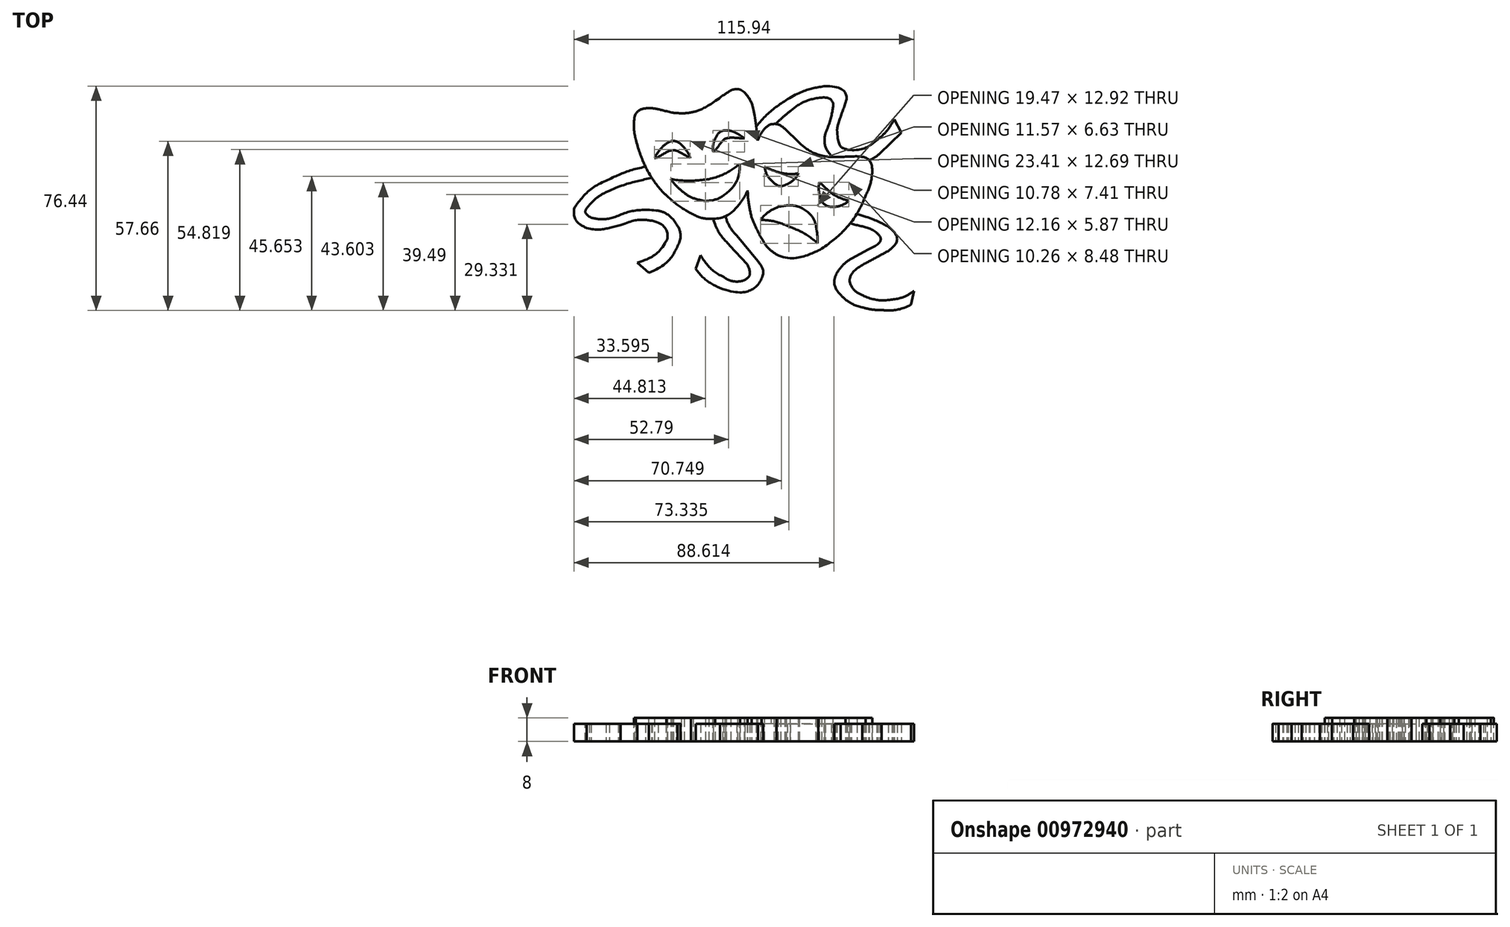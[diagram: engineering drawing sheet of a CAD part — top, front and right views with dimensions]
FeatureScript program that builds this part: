
annotation { "Feature Type Name" : "Feature", "Feature Type Description" : "" }
export const myFeature = defineFeature(function(context is Context, id is Id, definition is map)
    precondition{}
    {
        {
            var Q0;
            Q0=qCreatedBy(makeId("Top.planeOp"),FACE);
            var sketch = newSketch(context, id + "F0", { "sketchPlane" : qUnion([Q0])});
            skFitSpline(sketch, "E0", {"points": [v(-36.35, 12.89) * mm, v(-41.05, 10.12) * mm], "startDerivative": vector(-3.86, -0.6) * mm, "endDerivative": vector(-3.7, -8.46) * mm});
            skFitSpline(sketch, "E1", {"points": [v(-36.35, 12.89) * mm, v(-28.3, 11.3) * mm], "startDerivative": vector(6.38, 0) * mm, "endDerivative": vector(11.28, -3.12) * mm});
            skFitSpline(sketch, "E2", {"points": [v(-28.3, 11.3) * mm, v(-21.02, 11.6) * mm], "startDerivative": vector(6.97, -0.45) * mm, "endDerivative": vector(7.42, 2.23) * mm});
            skFitSpline(sketch, "E3", {"points": [v(-21.02, 11.6) * mm, v(-10.98, 17.14) * mm], "startDerivative": vector(5.93, 0.6) * mm, "endDerivative": vector(14.84, 11.13) * mm});
            skFitSpline(sketch, "E4", {"points": [v(-10.98, 17.14) * mm, v(-3.61, 18.33) * mm], "startDerivative": vector(6.53, 3.86) * mm, "endDerivative": vector(9.64, -7.27) * mm});
            skFitSpline(sketch, "E5", {"points": [v(-3.61, 18.33) * mm, v(0.49, 5.72) * mm], "startDerivative": vector(7.71, -9.5) * mm, "endDerivative": vector(2.67, -25.37) * mm});
            skFitSpline(sketch, "E6", {"points": [v(0.49, 5.72) * mm, v(-0.6, -9.66) * mm], "startDerivative": vector(2.52, -15.28) * mm, "endDerivative": vector(-5.04, -15.58) * mm});
            skFitSpline(sketch, "E7", {"points": [v(-0.6, -9.66) * mm, v(-5.05, -19.55) * mm], "startDerivative": vector(-3.26, -11.13) * mm, "endDerivative": vector(-6.97, -9.05) * mm});
            skFitSpline(sketch, "E8", {"points": [v(-5.05, -19.55) * mm, v(-13.56, -24.85) * mm], "startDerivative": vector(-6.38, -7.57) * mm, "endDerivative": vector(-14.24, -1.48) * mm});
            skFitSpline(sketch, "E9", {"points": [v(-13.56, -24.85) * mm, v(-21.86, -22.92) * mm], "startDerivative": vector(-8.75, -0.45) * mm, "endDerivative": vector(-9.2, 5.79) * mm});
            skFitSpline(sketch, "E10", {"points": [v(-21.86, -22.92) * mm, v(-30.27, -16.83) * mm], "startDerivative": vector(-7.57, 3.56) * mm, "endDerivative": vector(-9.35, 8.75) * mm});
            skFitSpline(sketch, "E11", {"points": [v(-30.27, -16.83) * mm, v(-36.85, -8.08) * mm], "startDerivative": vector(-5.2, 4.6) * mm, "endDerivative": vector(-7.71, 14.24) * mm});
            skFitSpline(sketch, "E12", {"points": [v(-36.85, -8.08) * mm, v(-40.66, 2.26) * mm], "startDerivative": vector(-2.23, 4.15) * mm, "endDerivative": vector(-3.41, 14.4) * mm});
            skFitSpline(sketch, "E13", {"points": [v(-40.66, 2.26) * mm, v(-41.05, 10.12) * mm], "startDerivative": vector(-0.6, 1.78) * mm, "endDerivative": vector(1.78, 13.2) * mm});
            skSolve(sketch);
        }
        {
            var Q0;
            Q0=qCreatedBy(makeId("Top.planeOp"),FACE);
            var sketch = newSketch(context, id + "F1", { "sketchPlane" : qUnion([Q0])});
            skFitSpline(sketch, "E14", {"points": [v(-34.23, -4.2) * mm, v(-29.9, 0.99) * mm], "startDerivative": vector(3.98, 9.03) * mm, "endDerivative": vector(1.64, 0.6) * mm});
            skFitSpline(sketch, "E15", {"points": [v(-29.9, 0.99) * mm, v(-25.1, 0.39) * mm], "startDerivative": vector(6.69, 4.94) * mm, "endDerivative": vector(1.32, -1.72) * mm});
            skFitSpline(sketch, "E16", {"points": [v(-25.1, 0.39) * mm, v(-22.07, -4.1) * mm], "startDerivative": vector(4.23, -3.83) * mm, "endDerivative": vector(1.19, -3.97) * mm});
            skFitSpline(sketch, "E17", {"points": [v(-22.07, -4.1) * mm, v(-27.75, -1.5) * mm], "startDerivative": vector(-7.14, 3.44) * mm, "endDerivative": vector(-3.57, -0.53) * mm});
            skFitSpline(sketch, "E18", {"points": [v(-27.75, -1.5) * mm, v(-34.23, -4.2) * mm], "startDerivative": vector(-5.15, 1.19) * mm, "endDerivative": vector(-5.7, -0.83) * mm});
            skFitSpline(sketch, "E19", {"points": [v(-14.22, -2.12) * mm, v(-13.52, 2.55) * mm], "startDerivative": vector(-0.66, 2.51) * mm, "endDerivative": vector(2.78, 4.76) * mm});
            skFitSpline(sketch, "E20", {"points": [v(-13.52, 2.55) * mm, v(-10.26, 5.23) * mm], "startDerivative": vector(3.04, 7.14) * mm, "endDerivative": vector(2.78, 0) * mm});
            skFitSpline(sketch, "E21", {"points": [v(-10.26, 5.23) * mm, v(-5.94, 4.18) * mm], "startDerivative": vector(4.36, 0.66) * mm, "endDerivative": vector(3.83, -2.25) * mm});
            skFitSpline(sketch, "E22", {"points": [v(-5.94, 4.18) * mm, v(-3.56, 2.55) * mm], "startDerivative": vector(2.64, -1.72) * mm, "endDerivative": vector(2.38, -1.63) * mm});
            skFitSpline(sketch, "E23", {"points": [v(-3.56, 2.55) * mm, v(-9.82, 2.55) * mm], "startDerivative": vector(-6.26, 0) * mm, "endDerivative": vector(-5.68, -1.72) * mm});
            skFitSpline(sketch, "E24", {"points": [v(-9.82, 2.55) * mm, v(-14.22, -2.12) * mm], "startDerivative": vector(-3.83, -0.4) * mm, "endDerivative": vector(-3.17, -1.85) * mm});
            skFitSpline(sketch, "E25", {"points": [v(-28.63, -11.29) * mm, v(-15.72, -11.33) * mm], "startDerivative": vector(12.95, -2.78) * mm, "endDerivative": vector(13.48, 1.85) * mm});
            skFitSpline(sketch, "E26", {"points": [v(-15.72, -11.33) * mm, v(-5.23, -6.13) * mm], "startDerivative": vector(14.8, 3.3) * mm, "endDerivative": vector(8.72, 7.14) * mm});
            skFitSpline(sketch, "E27", {"points": [v(-5.23, -6.13) * mm, v(-8.27, -14.81) * mm], "startDerivative": vector(1.06, -15.2) * mm, "endDerivative": vector(-2.9, -2.51) * mm});
            skFitSpline(sketch, "E28", {"points": [v(-8.27, -14.81) * mm, v(-16.87, -18.82) * mm], "startDerivative": vector(-9.25, -9.12) * mm, "endDerivative": vector(-11.37, -0.8) * mm});
            skFitSpline(sketch, "E29", {"points": [v(-16.87, -18.82) * mm, v(-24.18, -16) * mm], "startDerivative": vector(-13.22, 2.25) * mm, "endDerivative": vector(-5.55, 4.1) * mm});
            skFitSpline(sketch, "E30", {"points": [v(-24.18, -16) * mm, v(-28.63, -11.29) * mm], "startDerivative": vector(-6.87, 5.55) * mm, "endDerivative": vector(-2.38, 4.23) * mm});
            skSolve(sketch);
        }
        {
            var Q0;
            Q0=qCreatedBy(makeId("Top.planeOp"),FACE);
            var sketch = newSketch(context, id + "F2", { "sketchPlane" : qUnion([Q0])});
            skFitSpline(sketch, "E31", {"points": [v(5.5, 7.38) * mm, v(0.42, 0.67) * mm], "startDerivative": vector(-8.96, -3.46) * mm, "endDerivative": vector(-2.68, -6.3) * mm});
            skFitSpline(sketch, "E32", {"points": [v(0.42, 0.67) * mm, v(-2.35, -11.38) * mm], "startDerivative": vector(-5.97, -11.78) * mm, "endDerivative": vector(-0.79, -6.9) * mm});
            skFitSpline(sketch, "E33", {"points": [v(-2.35, -11.38) * mm, v(-1.13, -24.42) * mm], "startDerivative": vector(-1.41, -14.94) * mm, "endDerivative": vector(2.87, -10.99) * mm});
            skFitSpline(sketch, "E34", {"points": [v(-1.13, -24.42) * mm, v(2.25, -31.53) * mm], "startDerivative": vector(3.39, -7.1) * mm, "endDerivative": vector(4.86, -8.1) * mm});
            skFitSpline(sketch, "E35", {"points": [v(2.25, -31.53) * mm, v(7.36, -37.02) * mm], "startDerivative": vector(5.83, -10.76) * mm, "endDerivative": vector(5.88, -4) * mm});
            skFitSpline(sketch, "E36", {"points": [v(7.36, -37.02) * mm, v(21.6, -35.7) * mm], "startDerivative": vector(17.86, -9.21) * mm, "endDerivative": vector(7.86, 3.3) * mm});
            skFitSpline(sketch, "E37", {"points": [v(21.6, -35.7) * mm, v(30.84, -28.25) * mm], "startDerivative": vector(13.83, 8.02) * mm, "endDerivative": vector(1.5, 2.67) * mm});
            skFitSpline(sketch, "E38", {"points": [v(30.84, -28.25) * mm, v(37.73, -16.99) * mm], "startDerivative": vector(12.49, 13.2) * mm, "endDerivative": vector(3.14, 8.02) * mm});
            skFitSpline(sketch, "E39", {"points": [v(37.73, -16.99) * mm, v(39.98, -8.66) * mm], "startDerivative": vector(4.4, 8.33) * mm, "endDerivative": vector(0, 7.23) * mm});
            skFitSpline(sketch, "E40", {"points": [v(39.98, -8.66) * mm, v(34.85, -3.58) * mm], "startDerivative": vector(0.79, 16.5) * mm, "endDerivative": vector(-2.83, 0.47) * mm});
            skFitSpline(sketch, "E41", {"points": [v(34.85, -3.58) * mm, v(23.74, -3.58) * mm], "startDerivative": vector(-11.42, 0) * mm, "endDerivative": vector(-10.85, 1.57) * mm});
            skFitSpline(sketch, "E42", {"points": [v(23.74, -3.58) * mm, v(14.94, 1.14) * mm], "startDerivative": vector(-13.2, 2.83) * mm, "endDerivative": vector(-6.76, 5.97) * mm});
            skFitSpline(sketch, "E43", {"points": [v(14.94, 1.14) * mm, v(10.12, 5.9) * mm], "startDerivative": vector(-4.82, 4.77) * mm, "endDerivative": vector(-4.82, 4.77) * mm});
            skFitSpline(sketch, "E44", {"points": [v(10.12, 5.9) * mm, v(5.5, 7.38) * mm], "startDerivative": vector(-4.09, 3.46) * mm, "endDerivative": vector(-7.07, -1.1) * mm});
            skSolve(sketch);
        }
        {
            var Q0;
            Q0=qCreatedBy(makeId("Top.planeOp"),FACE);
            var sketch = newSketch(context, id + "F3", { "sketchPlane" : qUnion([Q0])});
            skFitSpline(sketch, "E45", {"points": [v(3.22, -7.11) * mm, v(8.84, -9.23) * mm], "startDerivative": vector(4, -1.87) * mm, "endDerivative": vector(5.24, -1.25) * mm});
            skFitSpline(sketch, "E46", {"points": [v(8.84, -9.23) * mm, v(14.8, -9.36) * mm], "startDerivative": vector(7.36, -1.25) * mm, "endDerivative": vector(5.9, 1.25) * mm});
            skFitSpline(sketch, "E47", {"points": [v(14.8, -9.36) * mm, v(10.74, -13.2) * mm], "startDerivative": vector(-1.16, -3.62) * mm, "endDerivative": vector(-7.39, -3.68) * mm});
            skFitSpline(sketch, "E48", {"points": [v(10.74, -13.2) * mm, v(6.5, -12.68) * mm], "startDerivative": vector(-4.21, -1.43) * mm, "endDerivative": vector(-5.64, 4.95) * mm});
            skFitSpline(sketch, "E49", {"points": [v(32, -18.66) * mm, v(26.55, -16.42) * mm], "startDerivative": vector(-7.24, 1.58) * mm, "endDerivative": vector(-4.63, 3.01) * mm});
            skFitSpline(sketch, "E50", {"points": [v(26.55, -16.42) * mm, v(21.98, -12.35) * mm], "startDerivative": vector(-5.1, 3.6) * mm, "endDerivative": vector(-4.4, 3.85) * mm});
            skFitSpline(sketch, "E51", {"points": [v(21.98, -12.35) * mm, v(22.77, -18.8) * mm], "startDerivative": vector(-1.73, -6.7) * mm, "endDerivative": vector(2.38, -3.75) * mm});
            skFitSpline(sketch, "E52", {"points": [v(22.77, -18.8) * mm, v(27.04, -20.83) * mm], "startDerivative": vector(3.11, -5.73) * mm, "endDerivative": vector(4.82, -0.1) * mm});
            skFitSpline(sketch, "E53", {"points": [v(27.04, -20.83) * mm, v(32, -18.66) * mm], "startDerivative": vector(6.28, 0.6) * mm, "endDerivative": vector(3, 3.53) * mm});
            skFitSpline(sketch, "E54", {"points": [v(1.86, -25.3) * mm, v(7.94, -20.83) * mm], "startDerivative": vector(6.1, 8.54) * mm, "endDerivative": vector(4.55, 1.9) * mm});
            skFitSpline(sketch, "E55", {"points": [v(7.94, -20.83) * mm, v(15.07, -20.84) * mm], "startDerivative": vector(10.17, 2.6) * mm, "endDerivative": vector(4.28, -1.72) * mm});
            skFitSpline(sketch, "E56", {"points": [v(20.69, -26.66) * mm, v(21.3, -33.2) * mm], "startDerivative": vector(2.25, -11.35) * mm, "endDerivative": vector(-0.16, -4.05) * mm});
            skFitSpline(sketch, "E57", {"points": [v(21.3, -33.2) * mm, v(11.93, -27.61) * mm], "startDerivative": vector(-8.7, 8.54) * mm, "endDerivative": vector(-9.69, 3.75) * mm});
            skFitSpline(sketch, "E58", {"points": [v(11.93, -27.61) * mm, v(1.86, -25.3) * mm], "startDerivative": vector(-10.52, 4.48) * mm, "endDerivative": vector(-9.96, -0.56) * mm});
            skFitSpline(sketch, "E59", {"points": [v(15.07, -20.84) * mm, v(20.69, -26.66) * mm], "startDerivative": vector(12.48, -5.49) * mm, "endDerivative": vector(2, -5.61) * mm});
            skFitSpline(sketch, "E60", {"points": [v(6.5, -12.68) * mm, v(3.22, -7.11) * mm], "startDerivative": vector(-6.86, 6.39) * mm, "endDerivative": vector(-1.9, 8.17) * mm});
            skSolve(sketch);
        }
        {
            var Q0;
            Q0 = qSketchRegion(id + "F0", true);
            extrude(context, id + "F4", {"entities" : qUnion([Q0]), "depth" : 8 * mm, "offsetDistance" : 25.4 * mm});
        }
        {
            var Q0;
            Q0 = qSketchRegion(id + "F1", true);
            extrude(context, id + "F5", {"entities" : qUnion([Q0]), "operationType" : NewBodyOperationType.REMOVE, "depth" : 25 * mm, "offsetDistance" : 25 * mm});
        }
        {
            var Q0;
            Q0 = qSketchRegion(id + "F2", true);
            extrude(context, id + "F6", {"entities" : qUnion([Q0]), "operationType" : NewBodyOperationType.ADD, "depth" : 8 * mm, "offsetDistance" : 25 * mm});
        }
        {
            var Q0;
            Q0 = qSketchRegion(id + "F3", true);
            extrude(context, id + "F7", {"entities" : qUnion([Q0]), "operationType" : NewBodyOperationType.REMOVE, "depth" : 25 * mm, "offsetDistance" : 25 * mm});
        }
        {
            var Q0;
            Q0=qCreatedBy(makeId("Top.planeOp"),FACE);
            var sketch = newSketch(context, id + "F8", { "sketchPlane" : qUnion([Q0])});
            skFitSpline(sketch, "E61", {"points": [v(33.8, -22.83) * mm, v(46.72, -28.6) * mm], "startDerivative": vector(21.4, -6.89) * mm, "endDerivative": vector(8.2, -6.74) * mm});
            skFitSpline(sketch, "E62", {"points": [v(33.8, -22.83) * mm, v(31.78, -26.2) * mm], "startDerivative": vector(-2.01, -3.38) * mm, "endDerivative": vector(-2.01, -3.38) * mm});
            skFitSpline(sketch, "E63", {"points": [v(31.78, -26.2) * mm, v(41.6, -29.65) * mm], "startDerivative": vector(9.81, -3.44) * mm, "endDerivative": vector(8.56, -6.85) * mm});
            skFitSpline(sketch, "E64", {"points": [v(41.6, -29.65) * mm, v(38.8, -35.24) * mm], "startDerivative": vector(5.35, -5.2) * mm, "endDerivative": vector(-15.81, -6.92) * mm});
            skFitSpline(sketch, "E65", {"points": [v(38.8, -35.24) * mm, v(32.88, -38.42) * mm], "startDerivative": vector(-5.91, -3.18) * mm, "endDerivative": vector(-5.91, -3.18) * mm});
            skFitSpline(sketch, "E66", {"points": [v(32.88, -38.42) * mm, v(27.75, -43.62) * mm], "startDerivative": vector(-6.06, -3.65) * mm, "endDerivative": vector(-4.53, -7.79) * mm});
            skFitSpline(sketch, "E67", {"points": [v(27.75, -43.62) * mm, v(29.18, -50.76) * mm], "startDerivative": vector(-2.48, -5.56) * mm, "endDerivative": vector(8.95, -8.88) * mm});
            skFitSpline(sketch, "E68", {"points": [v(29.18, -50.76) * mm, v(36.59, -55.05) * mm], "startDerivative": vector(5.27, -5.56) * mm, "endDerivative": vector(10.6, -2.28) * mm});
            skFitSpline(sketch, "E69", {"points": [v(36.59, -55.05) * mm, v(43.15, -56.03) * mm], "startDerivative": vector(7.12, -2.1) * mm, "endDerivative": vector(7.76, -0.17) * mm});
            skFitSpline(sketch, "E70", {"points": [v(43.15, -56.03) * mm, v(53.29, -54.08) * mm], "startDerivative": vector(7.12, 0.17) * mm, "endDerivative": vector(14.1, 7.87) * mm});
            skFitSpline(sketch, "E71", {"points": [v(53.29, -54.08) * mm, v(54.2, -49.53) * mm], "startDerivative": vector(0.9, 4.55) * mm, "endDerivative": vector(0.9, 4.55) * mm});
            skFitSpline(sketch, "E72", {"points": [v(54.2, -49.53) * mm, v(47.3, -52.32) * mm], "startDerivative": vector(-5.45, -3.35) * mm, "endDerivative": vector(-11.05, -1.3) * mm});
            skFitSpline(sketch, "E73", {"points": [v(47.3, -52.32) * mm, v(37.24, -51.22) * mm], "startDerivative": vector(-10.39, -1.54) * mm, "endDerivative": vector(-12.6, 5.29) * mm});
            skFitSpline(sketch, "E74", {"points": [v(37.24, -51.22) * mm, v(32.24, -46.15) * mm], "startDerivative": vector(-7.3, 3.9) * mm, "endDerivative": vector(-3.33, 10.86) * mm});
            skFitSpline(sketch, "E75", {"points": [v(32.24, -46.15) * mm, v(37.89, -39.91) * mm], "startDerivative": vector(0.27, 5.1) * mm, "endDerivative": vector(14.94, 7.7) * mm});
            skFitSpline(sketch, "E76", {"points": [v(37.89, -39.91) * mm, v(45.45, -35.84) * mm], "startDerivative": vector(7.8, 4.22) * mm, "endDerivative": vector(7.8, 4.22) * mm});
            skFitSpline(sketch, "E77", {"points": [v(45.45, -35.84) * mm, v(46.72, -28.6) * mm], "startDerivative": vector(2.63, 2.4) * mm, "endDerivative": vector(-12.6, 11.64) * mm});
            skSolve(sketch);
        }
        {
            var Q0;
            Q0=qCreatedBy(makeId("Top.planeOp"),FACE);
            var sketch = newSketch(context, id + "F9", { "sketchPlane" : qUnion([Q0])});
            skFitSpline(sketch, "E78", {"points": [v(-35.88, -6.89) * mm, v(-34.36, -10.54) * mm], "startDerivative": vector(1.51, -3.65) * mm, "endDerivative": vector(1.51, -3.65) * mm});
            skFitSpline(sketch, "E79", {"points": [v(-34.36, -10.54) * mm, v(-49.64, -15.3) * mm], "startDerivative": vector(-15.27, -4.76) * mm, "endDerivative": vector(-18.02, -8.7) * mm});
            skFitSpline(sketch, "E80", {"points": [v(-49.64, -15.3) * mm, v(-56.46, -20.17) * mm], "startDerivative": vector(-8.05, -3.3) * mm, "endDerivative": vector(-7, -8) * mm});
            skFitSpline(sketch, "E81", {"points": [v(-56.46, -20.17) * mm, v(-55.82, -24.45) * mm], "startDerivative": vector(-3.85, -4.52) * mm, "endDerivative": vector(9.79, -5.03) * mm});
            skFitSpline(sketch, "E82", {"points": [v(-55.82, -24.45) * mm, v(-46.62, -23.8) * mm], "startDerivative": vector(7.17, -2.08) * mm, "endDerivative": vector(11.72, 5.05) * mm});
            skFitSpline(sketch, "E83", {"points": [v(-46.62, -23.8) * mm, v(-32.98, -22.11) * mm], "startDerivative": vector(12.42, 5.57) * mm, "endDerivative": vector(18.18, -2.06) * mm});
            skFitSpline(sketch, "E84", {"points": [v(-32.98, -22.11) * mm, v(-26.92, -26.56) * mm], "startDerivative": vector(5.07, -1.21) * mm, "endDerivative": vector(5.93, -10.07) * mm});
            skFitSpline(sketch, "E85", {"points": [v(-26.92, -26.56) * mm, v(-26.35, -34.09) * mm], "startDerivative": vector(3.14, -3.82) * mm, "endDerivative": vector(-5.95, -10.78) * mm});
            skFitSpline(sketch, "E86", {"points": [v(-26.35, -34.09) * mm, v(-36.15, -43.3) * mm], "startDerivative": vector(-5.6, -11.3) * mm, "endDerivative": vector(-21.51, -9.4) * mm});
            skFitSpline(sketch, "E87", {"points": [v(-36.15, -43.3) * mm, v(-40.1, -39.84) * mm], "startDerivative": vector(-3.96, 3.47) * mm, "endDerivative": vector(-3.96, 3.47) * mm});
            skFitSpline(sketch, "E88", {"points": [v(-40.1, -39.84) * mm, v(-30.3, -32.53) * mm], "startDerivative": vector(8.04, 3.14) * mm, "endDerivative": vector(8.76, 16.68) * mm});
            skFitSpline(sketch, "E89", {"points": [v(-30.3, -32.53) * mm, v(-35.02, -25.53) * mm], "startDerivative": vector(2.27, 2.26) * mm, "endDerivative": vector(-18.88, 3.8) * mm});
            skFitSpline(sketch, "E90", {"points": [v(-35.02, -25.53) * mm, v(-45.8, -27.05) * mm], "startDerivative": vector(-9.61, 1.2) * mm, "endDerivative": vector(-17.66, -7.49) * mm});
            skFitSpline(sketch, "E91", {"points": [v(-45.8, -27.05) * mm, v(-57.4, -27.99) * mm], "startDerivative": vector(-12.94, -2.62) * mm, "endDerivative": vector(-14.68, 3.98) * mm});
            skFitSpline(sketch, "E92", {"points": [v(-57.4, -27.99) * mm, v(-61.53, -21.1) * mm], "startDerivative": vector(-6.3, 2.95) * mm, "endDerivative": vector(3.16, 13.72) * mm});
            skFitSpline(sketch, "E93", {"points": [v(-61.53, -21.1) * mm, v(-50.8, -11.89) * mm], "startDerivative": vector(7.18, 11.12) * mm, "endDerivative": vector(15.4, 5.92) * mm});
            skFitSpline(sketch, "E94", {"points": [v(-50.8, -11.89) * mm, v(-35.88, -6.89) * mm], "startDerivative": vector(14.34, 6.96) * mm, "endDerivative": vector(19.06, 2.8) * mm});
            skSolve(sketch);
        }
        {
            var Q0;
            Q0=qCreatedBy(makeId("Top.planeOp"),FACE);
            var sketch = newSketch(context, id + "F10", { "sketchPlane" : qUnion([Q0])});
            skFitSpline(sketch, "E95", {"points": [v(-0.84, 4.73) * mm, v(-1.49, -2.16) * mm], "startDerivative": vector(-0.65, -6.9) * mm, "endDerivative": vector(-0.65, -6.9) * mm});
            skFitSpline(sketch, "E96", {"points": [v(-1.49, -2.16) * mm, v(12.04, 11.86) * mm], "startDerivative": vector(11.3, 15.24) * mm, "endDerivative": vector(16.72, 13.47) * mm});
            skFitSpline(sketch, "E97", {"points": [v(12.04, 11.86) * mm, v(20.44, 16.16) * mm], "startDerivative": vector(6.87, 6.25) * mm, "endDerivative": vector(9.73, 1.81) * mm});
            skFitSpline(sketch, "E98", {"points": [v(20.44, 16.16) * mm, v(26.73, 14.2) * mm], "startDerivative": vector(12.96, 2.37) * mm, "endDerivative": vector(1.73, -6.51) * mm});
            skFitSpline(sketch, "E99", {"points": [v(26.73, 14.2) * mm, v(23.98, 4.12) * mm], "startDerivative": vector(-0.86, -9.03) * mm, "endDerivative": vector(-4.73, -10.92) * mm});
            skFitSpline(sketch, "E100", {"points": [v(23.98, 4.12) * mm, v(26.07, -3.4) * mm], "startDerivative": vector(-1.9, -8.13) * mm, "endDerivative": vector(7.07, -7) * mm});
            skFitSpline(sketch, "E101", {"points": [v(26.07, -3.4) * mm, v(32.25, -6.35) * mm], "startDerivative": vector(4.37, -3.7) * mm, "endDerivative": vector(8.43, -1.64) * mm});
            skFitSpline(sketch, "E102", {"points": [v(32.25, -6.35) * mm, v(42.57, -2.63) * mm], "startDerivative": vector(7.87, -0.31) * mm, "endDerivative": vector(11.19, 9.48) * mm});
            skFitSpline(sketch, "E103", {"points": [v(42.57, -2.63) * mm, v(49.97, 4.5) * mm], "startDerivative": vector(7.4, 7.13) * mm, "endDerivative": vector(7.4, 7.13) * mm});
            skFitSpline(sketch, "E104", {"points": [v(49.97, 4.5) * mm, v(47.53, 9.07) * mm], "startDerivative": vector(-2.44, 4.57) * mm, "endDerivative": vector(-2.44, 4.57) * mm});
            skFitSpline(sketch, "E105", {"points": [v(47.53, 9.07) * mm, v(41.93, 2.23) * mm], "startDerivative": vector(-6.89, -11.74) * mm, "endDerivative": vector(-9.91, -8.78) * mm});
            skFitSpline(sketch, "E106", {"points": [v(41.93, 2.23) * mm, v(31.55, -1.31) * mm], "startDerivative": vector(-5.96, -3.93) * mm, "endDerivative": vector(-19.22, 2.28) * mm});
            skFitSpline(sketch, "E107", {"points": [v(31.55, -1.31) * mm, v(28, 5.51) * mm], "startDerivative": vector(-5.45, 2.29) * mm, "endDerivative": vector(-0.79, 20.17) * mm});
            skFitSpline(sketch, "E108", {"points": [v(28, 5.51) * mm, v(30.87, 14.78) * mm], "startDerivative": vector(0.15, 4.77) * mm, "endDerivative": vector(2.86, 9.27) * mm});
            skFitSpline(sketch, "E109", {"points": [v(30.87, 14.78) * mm, v(23.47, 20.33) * mm], "startDerivative": vector(2.38, 5.22) * mm, "endDerivative": vector(-25.24, -1.26) * mm});
            skFitSpline(sketch, "E110", {"points": [v(23.47, 20.33) * mm, v(11.06, 15.86) * mm], "startDerivative": vector(-11.77, -2.06) * mm, "endDerivative": vector(-16.89, -10.47) * mm});
            skFitSpline(sketch, "E111", {"points": [v(11.06, 15.86) * mm, v(-0.84, 4.73) * mm], "startDerivative": vector(-13.3, -8.6) * mm, "endDerivative": vector(-11.6, -17.55) * mm});
            skSolve(sketch);
        }
        {
            var Q0;
            Q0=qCreatedBy(makeId("Top.planeOp"),FACE);
            var sketch = newSketch(context, id + "F11", { "sketchPlane" : qUnion([Q0])});
            skFitSpline(sketch, "E112", {"points": [v(-14.85, -22.73) * mm, v(-8.57, -33.94) * mm], "startDerivative": vector(4.97, -20.67) * mm, "endDerivative": vector(7.49, -7.99) * mm});
            skFitSpline(sketch, "E113", {"points": [v(-8.57, -33.94) * mm, v(-2.66, -40.36) * mm], "startDerivative": vector(5.91, -6.43) * mm, "endDerivative": vector(5.91, -6.43) * mm});
            skFitSpline(sketch, "E114", {"points": [v(-2.66, -40.36) * mm, v(-3.4, -45.7) * mm], "startDerivative": vector(5.54, -11.3) * mm, "endDerivative": vector(-4.17, -2.76) * mm});
            skFitSpline(sketch, "E115", {"points": [v(-10.7, -44.7) * mm, v(-18.56, -37.35) * mm], "startDerivative": vector(-12.2, 5.22) * mm, "endDerivative": vector(-6.1, 9.1) * mm});
            skFitSpline(sketch, "E116", {"points": [v(-18.56, -37.35) * mm, v(-20.23, -41.85) * mm], "startDerivative": vector(-1.67, -4.5) * mm, "endDerivative": vector(-1.67, -4.5) * mm});
            skFitSpline(sketch, "E117", {"points": [v(-20.23, -41.85) * mm, v(-11.93, -48.45) * mm], "startDerivative": vector(7.48, -11.02) * mm, "endDerivative": vector(10.5, -4.93) * mm});
            skFitSpline(sketch, "E118", {"points": [v(-11.93, -48.45) * mm, v(1.04, -47.34) * mm], "startDerivative": vector(23.89, -9.1) * mm, "endDerivative": vector(5.83, 5.8) * mm});
            skFitSpline(sketch, "E119", {"points": [v(1.04, -47.34) * mm, v(1.04, -39.35) * mm], "startDerivative": vector(8.9, 13.24) * mm, "endDerivative": vector(-5.01, 6.61) * mm});
            skFitSpline(sketch, "E120", {"points": [v(1.04, -39.35) * mm, v(-6.25, -30.63) * mm], "startDerivative": vector(-7.3, 8.72) * mm, "endDerivative": vector(-7.3, 8.72) * mm});
            skFitSpline(sketch, "E121", {"points": [v(-6.25, -30.63) * mm, v(-10.04, -22.54) * mm], "startDerivative": vector(-6.65, 6.89) * mm, "endDerivative": vector(0.56, 8) * mm});
            skFitSpline(sketch, "E122", {"points": [v(-10.04, -22.54) * mm, v(-14.85, -22.73) * mm], "startDerivative": vector(-4.81, -0.19) * mm, "endDerivative": vector(-4.81, -0.19) * mm});
            skFitSpline(sketch, "E123", {"points": [v(-10.7, -44.7) * mm, v(-3.4, -45.7) * mm], "startDerivative": vector(7.76, -5.5) * mm, "endDerivative": vector(6.94, 2.76) * mm});
            skSolve(sketch);
        }
        {
            var Q0;
            Q0 = qSketchRegion(id + "F8", true);
            extrude(context, id + "F12", {"entities" : qUnion([Q0]), "operationType" : NewBodyOperationType.ADD, "depth" : 6 * mm, "offsetDistance" : 25 * mm});
        }
        {
            var Q0;
            Q0 = qSketchRegion(id + "F9", true);
            extrude(context, id + "F13", {"entities" : qUnion([Q0]), "operationType" : NewBodyOperationType.ADD, "depth" : 6 * mm, "offsetDistance" : 25 * mm});
        }
        {
            var Q0;
            Q0 = qSketchRegion(id + "F10", true);
            extrude(context, id + "F14", {"entities" : qUnion([Q0]), "operationType" : NewBodyOperationType.ADD, "depth" : 6 * mm, "offsetDistance" : 25 * mm});
        }
        {
            var Q0;
            Q0 = qSketchRegion(id + "F11", true);
            extrude(context, id + "F15", {"entities" : qUnion([Q0]), "operationType" : NewBodyOperationType.ADD, "depth" : 6 * mm, "offsetDistance" : 25 * mm});
        }
    });
